FCSTD DOCUMENT  (FreeCAD 0.17R13125 (Git))
Label: phase_angle_scale_MTMF
License: All rights reserved
LicenseURL: http://en.wikipedia.org/wiki/All_rights_reserved
objects: App::Annotation×10, Sketcher::SketchObject×1, Drawing::FeatureViewPart×1, Drawing::FeaturePage×1, TechDraw::DrawSVGTemplate×1, TechDraw::DrawViewPart×1, TechDraw::DrawPage×1
note: 1 computed .brp shape members not serialized (recipe doc carries the construction recipe); baked Part::Feature solids carry a one-line shape summary decoded from their .brp

FEATURE [Sketcher::SketchObject] Sketch
  sketch-geometry (131):
    g0: Circle [constr] CenterX=0 CenterY=0 CenterZ=0 NormalX=0 NormalY=0 NormalZ=1 AngleXU=0 Radius=17
    g1: LineSegment [constr] StartX=28.55 StartY=23.4 StartZ=0 EndX=28.55 EndY=-76.6 EndZ=0
    g2: LineSegment [constr] StartX=28.55 StartY=-76.6 StartZ=0 EndX=-28.55 EndY=-76.6 EndZ=0
    g3: LineSegment [constr] StartX=-28.55 StartY=-76.6 StartZ=0 EndX=-28.55 EndY=23.4 EndZ=0
    g4: ArcOfCircle CenterX=0 CenterY=0 CenterZ=0 NormalX=0 NormalY=0 NormalZ=1 AngleXU=0 Radius=18 StartAngle=0.312037 EndAngle=2.82956
    g5: LineSegment [constr] StartX=28.55 StartY=23.4 StartZ=0 EndX=9 EndY=35.4 EndZ=0
    g6: LineSegment [constr] StartX=9 StartY=35.4 StartZ=0 EndX=-9 EndY=35.4 EndZ=0
    g7: LineSegment [constr] StartX=-9 StartY=35.4 StartZ=0 EndX=-28.55 EndY=23.4 EndZ=0
    g8: LineSegment StartX=17.1308 StartY=5.52596 StartZ=0 EndX=31.4064 EndY=10.1309 EndZ=0
    g9: LineSegment StartX=-17.1308 StartY=5.52596 StartZ=0 EndX=-31.4064 EndY=10.1309 EndZ=0
    g10: ArcOfCircle CenterX=0 CenterY=0 CenterZ=0 NormalX=0 NormalY=0 NormalZ=1 AngleXU=0 Radius=33 StartAngle=0.312037 EndAngle=2.82956
    g11: Circle CenterX=21.7676 CenterY=13.2823 CenterZ=0 NormalX=0 NormalY=0 NormalZ=1 AngleXU=0 Radius=1.5
    g12: ArcOfCircle [constr] CenterX=0 CenterY=0 CenterZ=0 NormalX=0 NormalY=0 NormalZ=1 AngleXU=0 Radius=25.5 StartAngle=0.312037 EndAngle=2.82956
    g13: Circle CenterX=21.7676 CenterY=13.2823 CenterZ=0 NormalX=0 NormalY=0 NormalZ=1 AngleXU=0 Radius=3
    g14: Circle CenterX=-21.7676 CenterY=13.2823 CenterZ=0 NormalX=0 NormalY=0 NormalZ=1 AngleXU=0 Radius=1.5
    g15: Circle CenterX=-21.7676 CenterY=13.2823 CenterZ=0 NormalX=0 NormalY=0 NormalZ=1 AngleXU=0 Radius=3
    g16: LineSegment [constr] StartX=0 StartY=0 StartZ=0 EndX=23.3345 EndY=23.3345 EndZ=0
    g17: LineSegment [constr] StartX=0 StartY=0 StartZ=0 EndX=18.928 EndY=27.032 EndZ=0
    g18: LineSegment [constr] StartX=0 StartY=0 StartZ=0 EndX=13.9464 EndY=29.9082 EndZ=0
    g19: LineSegment [constr] StartX=0 StartY=0 StartZ=0 EndX=8.54103 EndY=31.8756 EndZ=0
    g20: LineSegment [constr] StartX=2.87614 StartY=32.8744 StartZ=0 EndX=0 EndY=0 EndZ=0
    g21: LineSegment [constr] StartX=-2.87614 StartY=32.8744 StartZ=0 EndX=0 EndY=0 EndZ=0
    g22: LineSegment StartX=13.435 StartY=13.435 StartZ=0 EndX=22.6274 EndY=22.6274 EndZ=0
    g23: ArcOfCircle [constr] CenterX=0 CenterY=0 CenterZ=0 NormalX=0 NormalY=0 NormalZ=1 AngleXU=0 Radius=19 StartAngle=0.312037 EndAngle=2.82956
    g24: ArcOfCircle [constr] CenterX=0 CenterY=0 CenterZ=0 NormalX=0 NormalY=0 NormalZ=1 AngleXU=0 Radius=32 StartAngle=0.312037 EndAngle=2.82956
    g25: LineSegment StartX=10.898 StartY=15.5639 StartZ=0 EndX=18.3544 EndY=26.2129 EndZ=0
    g26: LineSegment StartX=13.5238 StartY=29.0018 StartZ=0 EndX=8.02975 EndY=17.2198 EndZ=0
    g27: LineSegment StartX=8.28221 StartY=30.9096 StartZ=0 EndX=4.91756 EndY=18.3526 EndZ=0
    g28: LineSegment StartX=1.65596 StartY=18.9277 StartZ=0 EndX=2.78898 EndY=31.8782 EndZ=0
    g29: LineSegment StartX=-1.65596 StartY=18.9277 StartZ=0 EndX=-2.78898 EndY=31.8782 EndZ=0
    g30: LineSegment [constr] StartX=-8.54103 StartY=31.8756 StartZ=0 EndX=0 EndY=0 EndZ=0
    g31: LineSegment [constr] StartX=0 StartY=0 StartZ=0 EndX=-13.9464 EndY=29.9082 EndZ=0
    g32: LineSegment [constr] StartX=-18.928 StartY=27.032 StartZ=0 EndX=0 EndY=0 EndZ=0
    g33: LineSegment [constr] StartX=-23.3345 StartY=23.3345 StartZ=0 EndX=0 EndY=0 EndZ=0
    g34: LineSegment StartX=-8.28221 StartY=30.9096 StartZ=0 EndX=-4.91756 EndY=18.3526 EndZ=0
    g35: LineSegment StartX=-13.5238 StartY=29.0018 StartZ=0 EndX=-8.02975 EndY=17.2198 EndZ=0
    g36: LineSegment StartX=-18.3544 StartY=26.2129 StartZ=0 EndX=-10.898 EndY=15.5639 EndZ=0
    g37: LineSegment StartX=-22.6274 StartY=22.6274 StartZ=0 EndX=-13.435 EndY=13.435 EndZ=0
    g38: ArcOfCircle [constr] CenterX=0 CenterY=0 CenterZ=0 NormalX=0 NormalY=0 NormalZ=1 AngleXU=0 Radius=22 StartAngle=0.312037 EndAngle=2.82956
    g39: ArcOfCircle [constr] CenterX=0 CenterY=0 CenterZ=0 NormalX=0 NormalY=0 NormalZ=1 AngleXU=0 Radius=29 StartAngle=0.312037 EndAngle=2.82956
    g40: ArcOfCircle [constr] CenterX=0 CenterY=0 CenterZ=0 NormalX=0 NormalY=0 NormalZ=1 AngleXU=0 Radius=20 StartAngle=0.312037 EndAngle=2.82956
    g41: ArcOfCircle [constr] CenterX=0 CenterY=0 CenterZ=0 NormalX=0 NormalY=0 NormalZ=1 AngleXU=0 Radius=31 StartAngle=0.312037 EndAngle=2.82956
    g42: LineSegment StartX=12.8558 StartY=15.3209 StartZ=0 EndX=19.9264 EndY=23.7474 EndZ=0
    g43: LineSegment StartX=10 StartY=17.3205 StartZ=0 EndX=15.5 EndY=26.8468 EndZ=0
    g44: LineSegment StartX=6.8404 StartY=18.7939 StartZ=0 EndX=10.6026 EndY=29.1305 EndZ=0
    g45: LineSegment StartX=3.47296 StartY=19.6962 StartZ=0 EndX=5.38309 EndY=30.529 EndZ=0
    g46: LineSegment StartX=0 StartY=20 StartZ=0 EndX=0 EndY=31 EndZ=0
    g47: LineSegment StartX=-3.47296 StartY=19.6962 StartZ=0 EndX=-5.38309 EndY=30.529 EndZ=0
    g48: LineSegment StartX=-6.8404 StartY=18.7939 StartZ=0 EndX=-10.6026 EndY=29.1305 EndZ=0
    g49: LineSegment StartX=-10 StartY=17.3205 StartZ=0 EndX=-15.5 EndY=26.8468 EndZ=0
    g50: LineSegment StartX=-12.8558 StartY=15.3209 StartZ=0 EndX=-19.9264 EndY=23.7474 EndZ=0
    g51: LineSegment StartX=15.2825 StartY=15.8255 StartZ=0 EndX=20.1451 EndY=20.8609 EndZ=0
    g52: LineSegment StartX=15.004 StartY=16.0898 StartZ=0 EndX=19.778 EndY=21.2093 EndZ=0
    g53: LineSegment StartX=14.7209 StartY=16.3492 StartZ=0 EndX=19.4048 EndY=21.5512 EndZ=0
    g54: LineSegment StartX=14.4333 StartY=16.6036 StartZ=0 EndX=19.0257 EndY=21.8866 EndZ=0
    g55: LineSegment StartX=13.845 StartY=17.0972 StartZ=0 EndX=18.2503 EndY=22.5372 EndZ=0
    g56: LineSegment StartX=13.5446 StartY=17.3362 StartZ=0 EndX=17.8542 EndY=22.8523 EndZ=0
    g57: LineSegment StartX=13.2399 StartY=17.57 StartZ=0 EndX=17.4526 EndY=23.1604 EndZ=0
    g58: LineSegment StartX=12.9313 StartY=17.7984 StartZ=0 EndX=17.0458 EndY=23.4615 EndZ=0
    g59: LineSegment StartX=12.3022 StartY=18.2388 StartZ=0 EndX=16.2166 EndY=24.0421 EndZ=0
    g60: LineSegment StartX=11.9821 StartY=18.4508 StartZ=0 EndX=15.7945 EndY=24.3214 EndZ=0
    g61: LineSegment StartX=11.6582 StartY=18.6571 StartZ=0 EndX=15.3677 EndY=24.5934 EndZ=0
    g62: LineSegment StartX=11.3308 StartY=18.8577 StartZ=0 EndX=14.9361 EndY=24.8579 EndZ=0
    g63: LineSegment StartX=10.6658 StartY=19.2416 StartZ=0 EndX=14.0595 EndY=25.364 EndZ=0
    g64: LineSegment StartX=10.3284 StartY=19.4248 StartZ=0 EndX=13.6147 EndY=25.6055 EndZ=0
    g65: LineSegment StartX=9.98779 StartY=19.6021 StartZ=0 EndX=13.1657 EndY=25.8392 EndZ=0
    g66: LineSegment StartX=9.64417 StartY=19.7735 StartZ=0 EndX=12.7128 EndY=26.065 EndZ=0
    g67: LineSegment StartX=8.94821 StartY=20.098 StartZ=0 EndX=11.7954 EndY=26.4928 EndZ=0
    g68: LineSegment StartX=8.59608 StartY=20.2511 StartZ=0 EndX=11.3312 EndY=26.6946 EndZ=0
    g69: LineSegment StartX=8.24135 StartY=20.398 StartZ=0 EndX=10.8636 EndY=26.8883 EndZ=0
    g70: LineSegment StartX=7.88409 StartY=20.5388 StartZ=0 EndX=10.3927 EndY=27.0738 EndZ=0
    g71: LineSegment StartX=7.1625 StartY=20.8014 StartZ=0 EndX=9.44148 EndY=27.42 EndZ=0
    g72: LineSegment StartX=6.79837 StartY=20.9232 StartZ=0 EndX=8.96149 EndY=27.5806 EndZ=0
    g73: LineSegment StartX=6.43218 StartY=21.0387 StartZ=0 EndX=8.47878 EndY=27.7328 EndZ=0
    g74: LineSegment StartX=6.06402 StartY=21.1478 StartZ=0 EndX=7.99348 EndY=27.8766 EndZ=0
    g75: LineSegment StartX=5.32228 StartY=21.3465 StartZ=0 EndX=7.01573 EndY=28.1386 EndZ=0
    g76: LineSegment StartX=4.94892 StartY=21.4361 StartZ=0 EndX=6.52358 EndY=28.2567 EndZ=0
    g77: LineSegment StartX=4.57406 StartY=21.5192 StartZ=0 EndX=6.02944 EndY=28.3663 EndZ=0
    g78: LineSegment StartX=4.1978 StartY=21.5958 StartZ=0 EndX=5.53346 EndY=28.4672 EndZ=0
    g79: LineSegment StartX=3.44156 StartY=21.7291 StartZ=0 EndX=4.5366 EndY=28.643 EndZ=0
    g80: LineSegment StartX=3.06181 StartY=21.7859 StartZ=0 EndX=4.03602 EndY=28.7178 EndZ=0
    g81: LineSegment StartX=2.68113 StartY=21.836 StartZ=0 EndX=3.53421 EndY=28.7838 EndZ=0
    g82: LineSegment StartX=2.29963 StartY=21.8795 StartZ=0 EndX=3.03133 EndY=28.8411 EndZ=0
    g83: LineSegment StartX=1.53464 StartY=21.9464 StartZ=0 EndX=2.02294 EndY=28.9294 EndZ=0
    g84: LineSegment StartX=1.15139 StartY=21.9698 StartZ=0 EndX=1.51774 EndY=28.9603 EndZ=0
    g85: LineSegment StartX=0.767789 StartY=21.9866 StartZ=0 EndX=1.01209 EndY=28.9823 EndZ=0
    g86: LineSegment StartX=0.383953 StartY=21.9966 StartZ=0 EndX=0.50612 EndY=28.9956 EndZ=0
    g87: LineSegment StartX=-0.383953 StartY=21.9966 StartZ=0 EndX=-0.50612 EndY=28.9956 EndZ=0
    g88: LineSegment StartX=-0.767789 StartY=21.9866 StartZ=0 EndX=-1.01209 EndY=28.9823 EndZ=0
    g89: LineSegment StartX=-1.15139 StartY=21.9698 StartZ=0 EndX=-1.51774 EndY=28.9603 EndZ=0
    g90: LineSegment StartX=-1.53464 StartY=21.9464 StartZ=0 EndX=-2.02294 EndY=28.9294 EndZ=0
    g91: LineSegment StartX=-2.29963 StartY=21.8795 StartZ=0 EndX=-3.03133 EndY=28.8411 EndZ=0
    g92: LineSegment StartX=-2.68113 StartY=21.836 StartZ=0 EndX=-3.53421 EndY=28.7838 EndZ=0
    g93: LineSegment StartX=-3.06181 StartY=21.7859 StartZ=0 EndX=-4.03602 EndY=28.7178 EndZ=0
    g94: LineSegment StartX=-3.44156 StartY=21.7291 StartZ=0 EndX=-4.5366 EndY=28.643 EndZ=0
    g95: LineSegment StartX=-4.1978 StartY=21.5958 StartZ=0 EndX=-5.53346 EndY=28.4672 EndZ=0
    g96: LineSegment StartX=-4.57406 StartY=21.5192 StartZ=0 EndX=-6.02944 EndY=28.3663 EndZ=0
    g97: LineSegment StartX=-4.94892 StartY=21.4361 StartZ=0 EndX=-6.52358 EndY=28.2567 EndZ=0
    g98: LineSegment StartX=-5.32228 StartY=21.3465 StartZ=0 EndX=-7.01573 EndY=28.1386 EndZ=0
    g99: LineSegment StartX=-6.06402 StartY=21.1478 StartZ=0 EndX=-7.99348 EndY=27.8766 EndZ=0
    g100: LineSegment StartX=-6.43218 StartY=21.0387 StartZ=0 EndX=-8.47878 EndY=27.7328 EndZ=0
    g101: LineSegment StartX=-6.79837 StartY=20.9232 StartZ=0 EndX=-8.96149 EndY=27.5806 EndZ=0
    g102: LineSegment StartX=-7.1625 StartY=20.8014 StartZ=0 EndX=-9.44148 EndY=27.42 EndZ=0
    g103: LineSegment StartX=-7.88409 StartY=20.5388 StartZ=0 EndX=-10.3927 EndY=27.0738 EndZ=0
    g104: LineSegment StartX=-8.24135 StartY=20.398 StartZ=0 EndX=-10.8636 EndY=26.8883 EndZ=0
    g105: LineSegment StartX=-8.59608 StartY=20.2511 StartZ=0 EndX=-11.3312 EndY=26.6946 EndZ=0
    g106: LineSegment StartX=-8.94821 StartY=20.098 StartZ=0 EndX=-11.7954 EndY=26.4928 EndZ=0
    g107: LineSegment StartX=-9.64417 StartY=19.7735 StartZ=0 EndX=-12.7128 EndY=26.065 EndZ=0
    g108: LineSegment StartX=-9.98779 StartY=19.6021 StartZ=0 EndX=-13.1657 EndY=25.8392 EndZ=0
    g109: LineSegment StartX=-10.3284 StartY=19.4248 StartZ=0 EndX=-13.6147 EndY=25.6055 EndZ=0
    g110: LineSegment StartX=-10.6658 StartY=19.2416 StartZ=0 EndX=-14.0595 EndY=25.364 EndZ=0
    g111: LineSegment StartX=-11.3308 StartY=18.8577 StartZ=0 EndX=-14.9361 EndY=24.8579 EndZ=0
    g112: LineSegment StartX=-11.6582 StartY=18.6571 StartZ=0 EndX=-15.3677 EndY=24.5934 EndZ=0
    g113: LineSegment StartX=-11.9821 StartY=18.4508 StartZ=0 EndX=-15.7945 EndY=24.3214 EndZ=0
    g114: LineSegment StartX=-12.3022 StartY=18.2388 StartZ=0 EndX=-16.2166 EndY=24.0421 EndZ=0
    g115: LineSegment StartX=-12.9313 StartY=17.7984 StartZ=0 EndX=-17.0458 EndY=23.4615 EndZ=0
    g116: LineSegment StartX=-13.2399 StartY=17.57 StartZ=0 EndX=-17.4526 EndY=23.1604 EndZ=0
    g117: LineSegment StartX=-13.5446 StartY=17.3362 StartZ=0 EndX=-17.8542 EndY=22.8523 EndZ=0
    g118: LineSegment StartX=-13.845 StartY=17.0972 StartZ=0 EndX=-18.2503 EndY=22.5372 EndZ=0
    g119: LineSegment StartX=-14.4333 StartY=16.6036 StartZ=0 EndX=-19.0257 EndY=21.8866 EndZ=0
    g120: LineSegment StartX=-14.7209 StartY=16.3492 StartZ=0 EndX=-19.4048 EndY=21.5512 EndZ=0
    g121: LineSegment StartX=-15.004 StartY=16.0898 StartZ=0 EndX=-19.778 EndY=21.2093 EndZ=0
    g122: LineSegment StartX=-15.2825 StartY=15.8255 StartZ=0 EndX=-20.1451 EndY=20.8609 EndZ=0
    g123: LineSegment StartX=-21.7676 StartY=13.2823 StartZ=0 EndX=-21.7676 EndY=16.2823 EndZ=0
    g124: LineSegment StartX=-21.7676 StartY=13.2823 StartZ=0 EndX=-21.7676 EndY=10.2823 EndZ=0
    g125: LineSegment StartX=-21.7676 StartY=13.2823 StartZ=0 EndX=-24.7676 EndY=13.2823 EndZ=0
    g126: LineSegment StartX=-21.7676 StartY=13.2823 StartZ=0 EndX=-18.7676 EndY=13.2823 EndZ=0
    g127: LineSegment StartX=18.7676 StartY=13.2823 StartZ=0 EndX=21.7676 EndY=13.2823 EndZ=0
    g128: LineSegment StartX=21.7676 StartY=13.2823 StartZ=0 EndX=21.7676 EndY=16.2823 EndZ=0
    g129: LineSegment StartX=21.7676 StartY=13.2823 StartZ=0 EndX=21.7676 EndY=10.2823 EndZ=0
    g130: LineSegment StartX=21.7676 StartY=13.2823 StartZ=0 EndX=24.7676 EndY=13.2823 EndZ=0
  constraints (487):
    c: Coincident(g0,g-1)
    c: Coincident(g1,g2)
    c: Coincident(g2,g3)
    c: Horizontal(g2)
    c: Vertical(g1)
    c: Vertical(g3)
    c: Symmetric(g3,g1,g-2)
    c: Radius(g0) = 17
    c: Distance(g2) = 57.1
    c: Distance(g3) = 100
    c: Coincident(g4,g-1)
    c: Coincident(g5,g1)
    c: Coincident(g6,g5)
    c: Horizontal(g6)
    c: Coincident(g7,g6)
    c: Coincident(g7,g3)
    c: Symmetric(g6,g5,g-2)
    c: Distance(g6) = 18
    c: Coincident(g8,g4)
    c: Coincident(g9,g4)
    c: Coincident(g10,g-1)
    c: Coincident(g10,g8)
    c: Distance(g-1,g4) = 18
    c: Perpendicular(g4,g9)
    c: Perpendicular(g4,g8)
    c: DistanceY(g4,g4) = 0
    c: Coincident(g12,g-1)
    c: PointOnObject(g12,g9)
    c: PointOnObject(g12,g8)
    c: Symmetric(g9,g4,g12)
    c: PointOnObject(g11,g12)
    c: Radius(g11) = 1.5
    c: Coincident(g11,g13)
    c: Radius(g13) = 3
    c: Distance(g11,g12) = 6
    c: Radius(g14) = 1.5
    c: Coincident(g14,g15)
    c: Radius(g15) = 3
    c: PointOnObject(g14,g12)
    c: Distance(g14,g12) = 6
    c: Coincident(g16,g-1)
    c: PointOnObject(g16,g10)
    c: Angle(g16,g-2) = 0.785398
    c: Distance(g11,g16) = 6
    c: PointOnObject(g17,g10)
    c: Angle(g16,g17) = 0.174533
    c: Coincident(g-1,g17)
    c: Coincident(g18,g-1)
    c: PointOnObject(g18,g10)
    c: Angle(g17,g18) = 0.174533
    c: Coincident(g19,g-1)
    c: PointOnObject(g19,g10)
    c: PointOnObject(g20,g10)
    c: Coincident(g20,g-1)
    c: Angle(g18,g19) = 0.174533
    c: Angle(g19,g20) = 0.174533
    c: PointOnObject(g21,g10)
    c: Coincident(g21,g-1)
    c: Angle(g20,g21) = 0.174533
    c: PointOnObject(g22,g16)
    c: PointOnObject(g22,g16)
    c: Coincident(g23,g-1)
    c: PointOnObject(g23,g8)
    c: PointOnObject(g23,g9)
    c: Coincident(g24,g-1)
    c: PointOnObject(g24,g8)
    c: PointOnObject(g24,g9)
    c: Distance(g23,g4) = 1
    c: Distance(g24,g8) = 1
    c: PointOnObject(g22,g23)
    c: PointOnObject(g22,g24)
    c: PointOnObject(g25,g17)
    c: PointOnObject(g25,g17)
    c: PointOnObject(g25,g24)
    c: PointOnObject(g25,g23)
    c: PointOnObject(g26,g18)
    c: PointOnObject(g26,g18)
    c: PointOnObject(g26,g23)
    c: PointOnObject(g26,g24)
    c: PointOnObject(g27,g19)
    c: PointOnObject(g27,g24)
    c: PointOnObject(g27,g23)
    c: PointOnObject(g27,g19)
    c: PointOnObject(g28,g20)
    c: PointOnObject(g28,g20)
    c: PointOnObject(g28,g24)
    c: PointOnObject(g28,g23)
    c: PointOnObject(g29,g21)
    c: PointOnObject(g29,g21)
    c: PointOnObject(g29,g24)
    c: PointOnObject(g29,g23)
    c: PointOnObject(g30,g10)
    c: Coincident(g30,g-1)
    c: Coincident(g31,g-1)
    c: PointOnObject(g31,g10)
    c: PointOnObject(g32,g10)
    c: Coincident(g32,g-1)
    c: Coincident(g33,g-1)
    c: PointOnObject(g33,g10)
    c: Angle(g21,g30) = 0.174533
    c: Angle(g30,g31) = 0.174533
    c: Angle(g31,g32) = 0.174533
    c: Angle(g32,g33) = 0.174533
    c: PointOnObject(g34,g30)
    c: PointOnObject(g34,g30)
    c: PointOnObject(g34,g23)
    c: PointOnObject(g34,g24)
    c: PointOnObject(g35,g31)
    c: PointOnObject(g35,g31)
    c: PointOnObject(g35,g23)
    c: PointOnObject(g35,g24)
    c: PointOnObject(g36,g32)
    c: PointOnObject(g36,g32)
    c: PointOnObject(g36,g23)
    c: PointOnObject(g36,g24)
    c: PointOnObject(g37,g33)
    c: PointOnObject(g37,g33)
    c: PointOnObject(g37,g23)
    c: PointOnObject(g37,g24)
    c: Coincident(g38,g-1)
    c: PointOnObject(g38,g8)
    c: PointOnObject(g38,g9)
    c: PointOnObject(g39,g8)
    c: PointOnObject(g39,g9)
    c: Coincident(g39,g-1)
    c: Coincident(g40,g-1)
    c: PointOnObject(g40,g8)
    c: PointOnObject(g40,g9)
    c: Coincident(g41,g-1)
    c: PointOnObject(g41,g8)
    c: PointOnObject(g41,g9)
    c: Distance(g39,g8) = 4
    c: Distance(g41,g8) = 2
    c: Distance(g38,g4) = 4
    c: Distance(g40,g4) = 2
    c: PointOnObject(g42,g40)
    c: PointOnObject(g42,g41)
    c: Perpendicular(g40,g42)
    c: Angle(g22,g42) = 0.0872665
    c: PointOnObject(g43,g40)
    c: PointOnObject(g43,g41)
    c: Perpendicular(g40,g43)
    c: Angle(g22,g43) = 0.261799
    c: PointOnObject(g44,g40)
    c: PointOnObject(g44,g41)
    c: Perpendicular(g40,g44)
    c: Angle(g22,g44) = 0.436332
    c: PointOnObject(g45,g40)
    c: PointOnObject(g45,g41)
    c: Perpendicular(g40,g45)
    c: Angle(g22,g45) = 0.610865
    c: PointOnObject(g46,g40)
    c: PointOnObject(g46,g41)
    c: Perpendicular(g40,g46)
    c: Angle(g22,g46) = 0.785398
    c: PointOnObject(g47,g40)
    c: PointOnObject(g47,g41)
    c: Perpendicular(g40,g47)
    c: Angle(g22,g47) = 0.959931
    c: PointOnObject(g48,g40)
    c: PointOnObject(g48,g41)
    c: Perpendicular(g40,g48)
    c: Angle(g22,g48) = 1.13446
    c: PointOnObject(g49,g40)
    c: PointOnObject(g49,g41)
    c: Perpendicular(g40,g49)
    c: Angle(g22,g49) = 1.309
    c: PointOnObject(g50,g40)
    c: PointOnObject(g50,g41)
    c: Perpendicular(g40,g50)
    c: Angle(g22,g50) = 1.48353
    c: Coincident(g10,g9)
    c: PointOnObject(g51,g38)
    c: PointOnObject(g51,g39)
    c: Perpendicular(g38,g51)
    c: Angle(g22,g51) = 0.0174533
    c: PointOnObject(g52,g38)
    c: PointOnObject(g52,g39)
    c: Perpendicular(g38,g52)
    c: Angle(g22,g52) = 0.0349066
    c: PointOnObject(g53,g38)
    c: PointOnObject(g53,g39)
    c: Perpendicular(g38,g53)
    c: Angle(g22,g53) = 0.0523599
    c: PointOnObject(g54,g38)
    c: PointOnObject(g54,g39)
    c: Perpendicular(g38,g54)
    c: Angle(g22,g54) = 0.0698132
    c: PointOnObject(g55,g38)
    c: PointOnObject(g55,g39)
    c: Perpendicular(g38,g55)
    c: Angle(g22,g55) = 0.10472
    c: PointOnObject(g56,g38)
    c: PointOnObject(g56,g39)
    c: Perpendicular(g38,g56)
    c: Angle(g22,g56) = 0.122173
    c: PointOnObject(g57,g38)
    c: PointOnObject(g57,g39)
    c: Perpendicular(g38,g57)
    c: Angle(g22,g57) = 0.139626
    c: PointOnObject(g58,g38)
    c: PointOnObject(g58,g39)
    c: Perpendicular(g38,g58)
    c: Angle(g22,g58) = 0.15708
    c: PointOnObject(g59,g38)
    c: PointOnObject(g59,g39)
    c: Perpendicular(g38,g59)
    c: Angle(g22,g59) = 0.191986
    c: PointOnObject(g60,g38)
    c: PointOnObject(g60,g39)
    c: Perpendicular(g38,g60)
    c: Angle(g22,g60) = 0.20944
    c: PointOnObject(g61,g38)
    c: PointOnObject(g61,g39)
    c: Perpendicular(g38,g61)
    c: Angle(g22,g61) = 0.226893
    c: PointOnObject(g62,g38)
    c: PointOnObject(g62,g39)
    c: Perpendicular(g38,g62)
    c: Angle(g22,g62) = 0.244346
    c: PointOnObject(g63,g38)
    c: PointOnObject(g63,g39)
    c: Perpendicular(g38,g63)
    c: Angle(g22,g63) = 0.279253
    c: PointOnObject(g64,g38)
    c: PointOnObject(g64,g39)
    c: Perpendicular(g38,g64)
    c: Angle(g22,g64) = 0.296706
    c: PointOnObject(g65,g38)
    c: PointOnObject(g65,g39)
    c: Perpendicular(g38,g65)
    c: Angle(g22,g65) = 0.314159
    c: PointOnObject(g66,g38)
    c: PointOnObject(g66,g39)
    c: Perpendicular(g38,g66)
    c: Angle(g22,g66) = 0.331613
    c: PointOnObject(g67,g38)
    c: PointOnObject(g67,g39)
    c: Perpendicular(g38,g67)
    c: Angle(g22,g67) = 0.366519
    c: PointOnObject(g68,g38)
    c: PointOnObject(g68,g39)
    c: Perpendicular(g38,g68)
    c: Angle(g22,g68) = 0.383972
    c: PointOnObject(g69,g38)
    c: PointOnObject(g69,g39)
    c: Perpendicular(g38,g69)
    c: Angle(g22,g69) = 0.401426
    c: PointOnObject(g70,g38)
    c: PointOnObject(g70,g39)
    c: Perpendicular(g38,g70)
    c: Angle(g22,g70) = 0.418879
    c: PointOnObject(g71,g38)
    c: PointOnObject(g71,g39)
    c: Perpendicular(g38,g71)
    c: Angle(g22,g71) = 0.453786
    c: PointOnObject(g72,g38)
    c: PointOnObject(g72,g39)
    c: Perpendicular(g38,g72)
    c: Angle(g22,g72) = 0.471239
    c: PointOnObject(g73,g38)
    c: PointOnObject(g73,g39)
    c: Perpendicular(g38,g73)
    c: Angle(g22,g73) = 0.488692
    c: PointOnObject(g74,g38)
    c: PointOnObject(g74,g39)
    c: Perpendicular(g38,g74)
    c: Angle(g22,g74) = 0.506145
    c: PointOnObject(g75,g38)
    c: PointOnObject(g75,g39)
    c: Perpendicular(g38,g75)
    c: Angle(g22,g75) = 0.541052
    c: PointOnObject(g76,g38)
    c: PointOnObject(g76,g39)
    c: Perpendicular(g38,g76)
    c: Angle(g22,g76) = 0.558505
    c: PointOnObject(g77,g38)
    c: PointOnObject(g77,g39)
    c: Perpendicular(g38,g77)
    c: Angle(g22,g77) = 0.575959
    c: PointOnObject(g78,g38)
    c: PointOnObject(g78,g39)
    c: Perpendicular(g38,g78)
    c: Angle(g22,g78) = 0.593412
    c: PointOnObject(g79,g38)
    c: PointOnObject(g79,g39)
    c: Perpendicular(g38,g79)
    c: Angle(g22,g79) = 0.628319
    c: PointOnObject(g80,g38)
    c: PointOnObject(g80,g39)
    c: Perpendicular(g38,g80)
    c: Angle(g22,g80) = 0.645772
    c: PointOnObject(g81,g38)
    c: PointOnObject(g81,g39)
    c: Perpendicular(g38,g81)
    c: Angle(g22,g81) = 0.663225
    c: PointOnObject(g82,g38)
    c: PointOnObject(g82,g39)
    c: Perpendicular(g38,g82)
    c: Angle(g22,g82) = 0.680678
    c: PointOnObject(g83,g38)
    c: PointOnObject(g83,g39)
    c: Perpendicular(g38,g83)
    c: Angle(g22,g83) = 0.715585
    c: PointOnObject(g84,g38)
    c: PointOnObject(g84,g39)
    c: Perpendicular(g38,g84)
    c: Angle(g22,g84) = 0.733038
    c: PointOnObject(g85,g38)
    c: PointOnObject(g85,g39)
    c: Perpendicular(g38,g85)
    c: Angle(g22,g85) = 0.750492
    c: PointOnObject(g86,g38)
    c: PointOnObject(g86,g39)
    c: Perpendicular(g38,g86)
    c: Angle(g22,g86) = 0.767945
    c: PointOnObject(g87,g38)
    c: PointOnObject(g87,g39)
    c: Perpendicular(g38,g87)
    c: Angle(g22,g87) = 0.802851
    c: PointOnObject(g88,g38)
    c: PointOnObject(g88,g39)
    c: Perpendicular(g38,g88)
    c: Angle(g22,g88) = 0.820305
    c: PointOnObject(g89,g38)
    c: PointOnObject(g89,g39)
    c: Perpendicular(g38,g89)
    c: Angle(g22,g89) = 0.837758
    c: PointOnObject(g90,g38)
    c: PointOnObject(g90,g39)
    c: Perpendicular(g38,g90)
    c: Angle(g22,g90) = 0.855211
    c: PointOnObject(g91,g38)
    c: PointOnObject(g91,g39)
    c: Perpendicular(g38,g91)
    c: Angle(g22,g91) = 0.890118
    c: PointOnObject(g92,g38)
    c: PointOnObject(g92,g39)
    c: Perpendicular(g38,g92)
    c: Angle(g22,g92) = 0.907571
    c: PointOnObject(g93,g38)
    c: PointOnObject(g93,g39)
    c: Perpendicular(g38,g93)
    c: Angle(g22,g93) = 0.925025
    c: PointOnObject(g94,g38)
    c: PointOnObject(g94,g39)
    c: Perpendicular(g38,g94)
    c: Angle(g22,g94) = 0.942478
    c: PointOnObject(g95,g38)
    c: PointOnObject(g95,g39)
    c: Perpendicular(g38,g95)
    c: Angle(g22,g95) = 0.977384
    c: PointOnObject(g96,g38)
    c: PointOnObject(g96,g39)
    c: Perpendicular(g38,g96)
    c: Angle(g22,g96) = 0.994838
    c: PointOnObject(g97,g38)
    c: PointOnObject(g97,g39)
    c: Perpendicular(g38,g97)
    c: Angle(g22,g97) = 1.01229
    c: PointOnObject(g98,g38)
    c: PointOnObject(g98,g39)
    c: Perpendicular(g38,g98)
    c: Angle(g22,g98) = 1.02974
    c: PointOnObject(g99,g38)
    c: PointOnObject(g99,g39)
    c: Perpendicular(g38,g99)
    c: Angle(g22,g99) = 1.06465
    c: PointOnObject(g100,g38)
    c: PointOnObject(g100,g39)
    c: Perpendicular(g38,g100)
    c: Angle(g22,g100) = 1.0821
    c: PointOnObject(g101,g38)
    c: PointOnObject(g101,g39)
    c: Perpendicular(g38,g101)
    c: Angle(g22,g101) = 1.09956
    c: PointOnObject(g102,g38)
    c: PointOnObject(g102,g39)
    c: Perpendicular(g38,g102)
    c: Angle(g22,g102) = 1.11701
    c: PointOnObject(g103,g38)
    c: PointOnObject(g103,g39)
    c: Perpendicular(g38,g103)
    c: Angle(g22,g103) = 1.15192
    c: PointOnObject(g104,g38)
    c: PointOnObject(g104,g39)
    c: Perpendicular(g38,g104)
    c: Angle(g22,g104) = 1.16937
    c: PointOnObject(g105,g38)
    c: PointOnObject(g105,g39)
    c: Perpendicular(g38,g105)
    c: Angle(g22,g105) = 1.18682
    c: PointOnObject(g106,g38)
    c: PointOnObject(g106,g39)
    c: Perpendicular(g38,g106)
    c: Angle(g22,g106) = 1.20428
    c: PointOnObject(g107,g38)
    c: PointOnObject(g107,g39)
    c: Perpendicular(g38,g107)
    c: Angle(g22,g107) = 1.23918
    c: PointOnObject(g108,g38)
    c: PointOnObject(g108,g39)
    c: Perpendicular(g38,g108)
    c: Angle(g22,g108) = 1.25664
    c: PointOnObject(g109,g38)
    c: PointOnObject(g109,g39)
    c: Perpendicular(g38,g109)
    c: Angle(g22,g109) = 1.27409
    c: PointOnObject(g110,g38)
    c: PointOnObject(g110,g39)
    c: Perpendicular(g38,g110)
    c: Angle(g22,g110) = 1.29154
    c: PointOnObject(g111,g38)
    c: PointOnObject(g111,g39)
    c: Perpendicular(g38,g111)
    c: Angle(g22,g111) = 1.32645
    c: PointOnObject(g112,g38)
    c: PointOnObject(g112,g39)
    c: Perpendicular(g38,g112)
    c: Angle(g22,g112) = 1.3439
    c: PointOnObject(g113,g38)
    c: PointOnObject(g113,g39)
    c: Perpendicular(g38,g113)
    c: Angle(g22,g113) = 1.36136
    c: PointOnObject(g114,g38)
    c: PointOnObject(g114,g39)
    c: Perpendicular(g38,g114)
    c: Angle(g22,g114) = 1.37881
    c: PointOnObject(g115,g38)
    c: PointOnObject(g115,g39)
    c: Perpendicular(g38,g115)
    c: Angle(g22,g115) = 1.41372
    c: PointOnObject(g116,g38)
    c: PointOnObject(g116,g39)
    c: Perpendicular(g38,g116)
    c: Angle(g22,g116) = 1.43117
    c: PointOnObject(g117,g38)
    c: PointOnObject(g117,g39)
    c: Perpendicular(g38,g117)
    c: Angle(g22,g117) = 1.44862
    c: PointOnObject(g118,g38)
    c: PointOnObject(g118,g39)
    c: Perpendicular(g38,g118)
    c: Angle(g22,g118) = 1.46608
    c: PointOnObject(g119,g38)
    c: PointOnObject(g119,g39)
    c: Perpendicular(g38,g119)
    c: Angle(g22,g119) = 1.50098
    c: PointOnObject(g120,g38)
    c: PointOnObject(g120,g39)
    c: Perpendicular(g38,g120)
    c: Angle(g22,g120) = 1.51844
    c: PointOnObject(g121,g38)
    c: PointOnObject(g121,g39)
    c: Perpendicular(g38,g121)
    c: Angle(g22,g121) = 1.53589
    c: PointOnObject(g122,g38)
    c: PointOnObject(g122,g39)
    c: Perpendicular(g38,g122)
    c: Angle(g22,g122) = 1.55334
    c: Radius(g10) = 33
    c: Distance(g-1,g6) = 35.4
    c: Coincident(g123,g14)
    c: PointOnObject(g123,g15)
    c: Vertical(g123)
    c: Coincident(g124,g14)
    c: PointOnObject(g124,g15)
    c: Vertical(g124)
    c: Coincident(g125,g14)
    c: PointOnObject(g125,g15)
    c: Horizontal(g125)
    c: Coincident(g126,g14)
    c: PointOnObject(g126,g15)
    c: Horizontal(g126)
    c: PointOnObject(g127,g13)
    c: Coincident(g127,g11)
    c: Horizontal(g127)
    c: Coincident(g128,g11)
    c: PointOnObject(g128,g13)
    c: Vertical(g128)
    c: Coincident(g129,g11)
    c: PointOnObject(g129,g13)
    c: Vertical(g129)
    c: Coincident(g130,g11)
    c: PointOnObject(g130,g13)
    c: Horizontal(g130)
    c: DistanceY(g3,g6) = 12
FEATURE [App::Annotation] Text001
  LabelText = 0
  Position = (37.5338,35.2074,0)
FEATURE [App::Annotation] Text
  LabelText = 10
  Position = (30.0736,40.4492,0)
FEATURE [App::Annotation] Text002
  LabelText = 20
  Position = (22.3973,45.683,0)
FEATURE [App::Annotation] Text003
  LabelText = 30
  Position = (13.6037,49.3764,0)
FEATURE [App::Annotation] Text004
  LabelText = 40
  Position = (4.64562,51.7018,0)
FEATURE [App::Annotation] Text005
  LabelText = 50
  Position = (-4.36823,52.0507,0)
FEATURE [App::Annotation] Text006
  LabelText = 60
  Position = (-13.7031,50.6368,0)
FEATURE [App::Annotation] Text007
  LabelText = 70
  Position = (-22.1635,47.9634,0)
FEATURE [App::Annotation] Text008
  LabelText = 80
  Position = (-30.0166,43.2184,0)
FEATURE [App::Annotation] Text009
  LabelText = 90
  Position = (-37.705,37.6812,0)
FEATURE [Drawing::FeatureViewPart] View
  Direction = (0,0,1)
  HiddenWidth = 0.15
  LineWidth = 0.35
  Rotation = 0
  ShowHiddenLines = false
  ShowSmoothLines = false
  Source = -> Sketch
  Tolerance = 0.05
  ViewResult = <blob: 6654 chars omitted>
  Visible = true
  X = 100
  Y = 100
FEATURE [Drawing::FeaturePage] Page
  EditableTexts = AUTHOR NAME | CREATION DATE | SUPERVISOR NAME | CHECK DATE | SCALE | WEIGHT | NUMBER | SHEET | TITLE | SUBTITLE
  Group = -> [View]
  Template = <path>
FEATURE [TechDraw::DrawSVGTemplate] Template
  EditableTexts = Designed_by_Name=Designed by Name; Drawing_number=Drawing number; FC-Date=Date; FC-SC=Scale; FC-SH=Sheet; FC-Title=Title; Subtitle=Subtitle; Weight=Weight
  Height = 210
  Orientation = 1
  Width = 297
FEATURE [TechDraw::DrawViewPart] View001
  ArcCenterMarks = true
  CenterScale = 2
  CoarseView = false
  Direction = (0,0,1)
  ExtraWidth = 1.4
  Focus = 100
  HardHidden = false
  HiddenWidth = 0.35
  HorizCenterLine = false
  IsoCount = 0
  IsoHidden = false
  IsoVisible = false
  IsoWidth = 0.5
  KeepLabel = false
  LineWidth = 0.2
  LockPosition = false
  Perspective = false
  Rotation = 0
  ScaleType = 0
  SeamHidden = false
  SeamVisible = false
  ShowSectionLine = true
  SmoothHidden = false
  SmoothVisible = false
  Source = -> [Sketch]
  VertCenterLine = false
  X = 148.5
  Y = 105
FEATURE [TechDraw::DrawPage] Page001
  KeepUpdated = true
  ProjectionType = 0
  Template = -> Template
  Views = -> [View001]
note: 1 file-system path scrubbed to <path> (originals preserved in the JSON sidecar)
